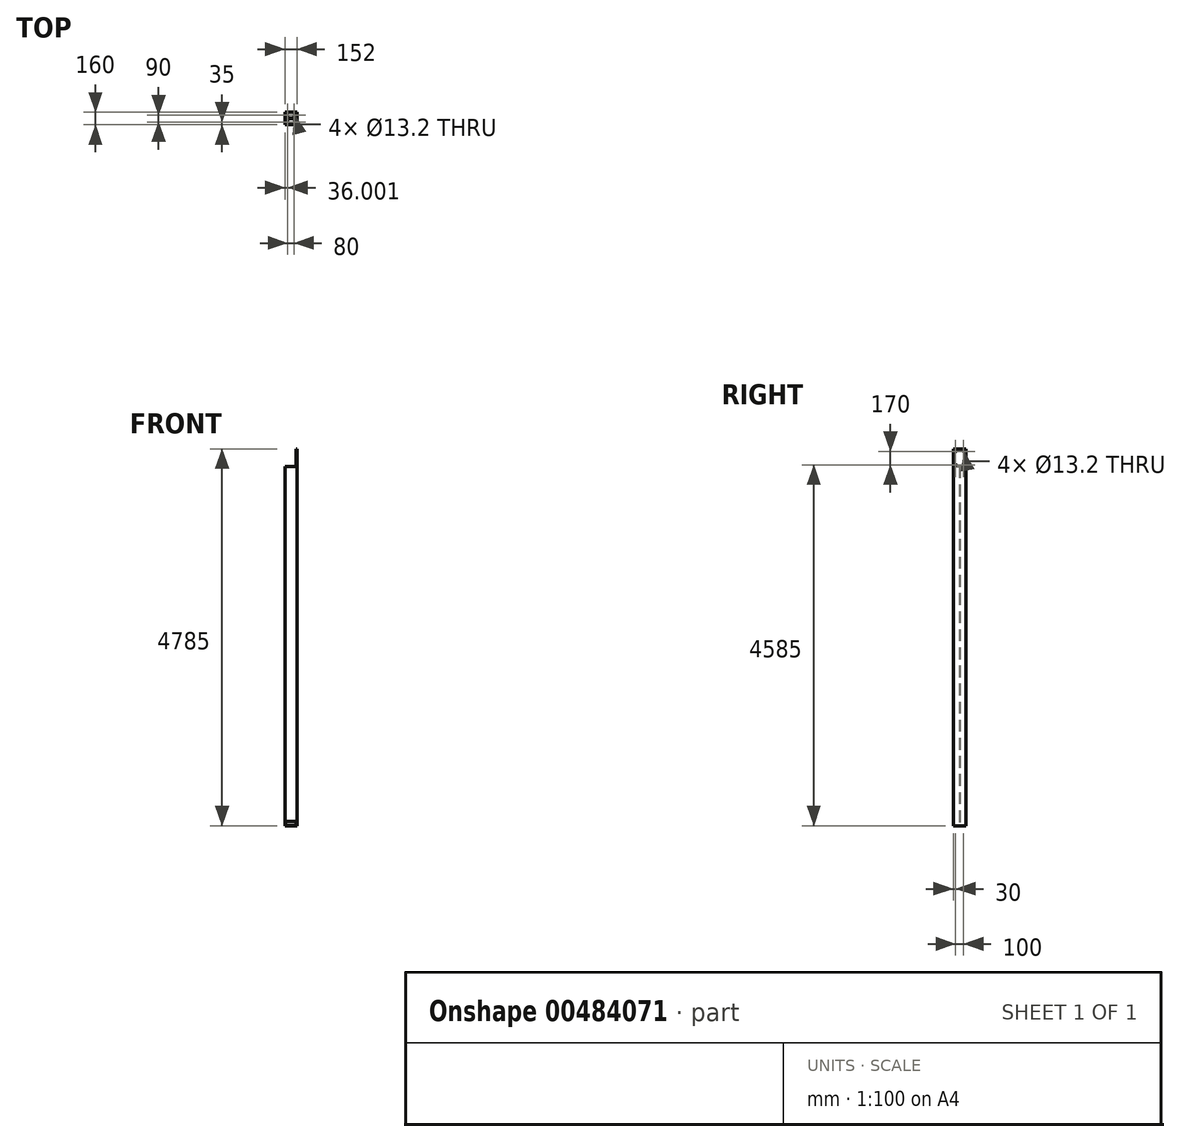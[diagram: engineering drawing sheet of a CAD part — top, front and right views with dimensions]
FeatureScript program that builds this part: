
annotation { "Feature Type Name" : "Feature", "Feature Type Description" : "" }
export const myFeature = defineFeature(function(context is Context, id is Id, definition is map)
    precondition{}
    {
        {
            var Q0;
            Q0=qCreatedBy(makeId("Top.planeOp"),FACE);
            var sketch = newSketch(context, id + "F0", { "sketchPlane" : qUnion([Q0])});
            skLineSegment(sketch, "E0", {"start": v(-170.58, -77) * mm, "end": v(-170.58, 83) * mm});
            skLineSegment(sketch, "E1", {"start": v(-170.58, 83) * mm, "end": v(-161.58, 83) * mm});
            skLineSegment(sketch, "E2", {"start": v(-161.58, 83) * mm, "end": v(-161.58, 6) * mm});
            skLineSegment(sketch, "E3", {"start": v(-161.58, 6) * mm, "end": v(-27.58, 6) * mm});
            skLineSegment(sketch, "E4", {"start": v(-27.58, 6) * mm, "end": v(-27.58, 83) * mm});
            skLineSegment(sketch, "E5", {"start": v(-27.58, 83) * mm, "end": v(-18.58, 83) * mm});
            skLineSegment(sketch, "E6", {"start": v(-18.58, 83) * mm, "end": v(-18.58, -77) * mm});
            skLineSegment(sketch, "E7", {"start": v(-18.58, -77) * mm, "end": v(-27.58, -77) * mm});
            skLineSegment(sketch, "E8", {"start": v(-27.58, -77) * mm, "end": v(-27.58, 0) * mm});
            skLineSegment(sketch, "E9", {"start": v(-27.58, 0) * mm, "end": v(-161.58, 0) * mm});
            skLineSegment(sketch, "E10", {"start": v(-161.58, 0) * mm, "end": v(-161.58, -77) * mm});
            skLineSegment(sketch, "E11", {"start": v(-161.58, -77) * mm, "end": v(-170.58, -77) * mm});
            skSolve(sketch);
        }
        {
            var Q0;
            Q0=qSketchRegion(id+"F0",true);
            extrude(context, id + "F1", {"entities" : qUnion([Q0]), "depth" : 4785 * mm, "offsetDistance" : 25 * mm});
        }
        {
            var Q0;
            Q0=makeQuery(id+"F1.opExtrude","SWEPT_FACE",FACE,{"disambiguationData":[OSD([sQuery(id+"F0.wireOp",EDGE,"E9")])]});
            var sketch = newSketch(context, id + "F2", { "sketchPlane" : qUnion([Q0])});
            skLineSegment(sketch, "E12.bottom", {"start": v(-161.58, 4785) * mm, "end": v(-27.58, 4785) * mm});
            skLineSegment(sketch, "E12.top", {"start": v(-161.58, 4565) * mm, "end": v(-27.58, 4565) * mm});
            skLineSegment(sketch, "E12.left", {"start": v(-161.58, 4785) * mm, "end": v(-161.58, 4565) * mm});
            skLineSegment(sketch, "E12.right", {"start": v(-27.58, 4785) * mm, "end": v(-27.58, 4565) * mm});
            skSolve(sketch);
        }
        {
            var Q0;
            Q0=qSketchRegion(id+"F2",true);
            extrude(context, id + "F3", {"entities" : qUnion([Q0]), "operationType" : NewBodyOperationType.REMOVE, "oppositeDirection" : true, "depth" : 100 * mm, "offsetDistance" : 25 * mm});
        }
        {
            var Q0;
            Q0=makeQuery(id+"F1.opExtrude","SWEPT_FACE",FACE,{"disambiguationData":[OSD([sQuery(id+"F0.wireOp",EDGE,"E0")])]});
            var sketch = newSketch(context, id + "F4", { "sketchPlane" : qUnion([Q0])});
            skLineSegment(sketch, "E13.bottom", {"start": v(-83, 4785) * mm, "end": v(77, 4785) * mm});
            skLineSegment(sketch, "E13.top", {"start": v(-83, 4565) * mm, "end": v(77, 4565) * mm});
            skLineSegment(sketch, "E13.left", {"start": v(-83, 4785) * mm, "end": v(-83, 4565) * mm});
            skLineSegment(sketch, "E13.right", {"start": v(77, 4785) * mm, "end": v(77, 4565) * mm});
            skSolve(sketch);
        }
        {
            var Q0;
            Q0=qSketchRegion(id+"F4",true);
            extrude(context, id + "F5", {"entities" : qUnion([Q0]), "operationType" : NewBodyOperationType.REMOVE, "oppositeDirection" : true, "depth" : 25 * mm, "offsetDistance" : 25 * mm});
        }
        {
            var Q0;
            Q0=makeQuery(id+"F1.opExtrude","SWEPT_FACE",FACE,{"disambiguationData":[OSD([sQuery(id+"F0.wireOp",EDGE,"E6")])]});
            var sketch = newSketch(context, id + "F6", { "sketchPlane" : qUnion([Q0])});
            skLineSegment(sketch, "E14", {"start": v(-77, 4785) * mm, "end": v(-47, 4785) * mm});
            skLineSegment(sketch, "E15", {"start": v(-47, 4785) * mm, "end": v(-47, 4755) * mm});
            skLineSegment(sketch, "E16", {"start": v(-47, 4755) * mm, "end": v(53, 4755) * mm});
            skLineSegment(sketch, "E17", {"start": v(53, 4755) * mm, "end": v(53, 4585) * mm});
            skLineSegment(sketch, "E18", {"start": v(53, 4585) * mm, "end": v(-47, 4585) * mm});
            skSolve(sketch);
        }
        {
            var Q0;
            Q0=sQuery(id+"F6.wireOp",VERTEX,"E16.start");
            var Q1;
            Q1=sQuery(id+"F6.wireOp",VERTEX,"E17.start");
            var Q2;
            Q2=sQuery(id+"F6.wireOp",VERTEX,"E18.end");
            var Q3;
            Q3=sQuery(id+"F6.wireOp",VERTEX,"E17.end");
            var Q4;
            Q4=makeQuery(id+"F1.opExtrude","SWEPT_BODY",BODY,{"disambiguationData":[OSD([sQuery(id+"F0.wireOp",EDGE,"E0"),sQuery(id+"F0.wireOp",EDGE,"E1"),sQuery(id+"F0.wireOp",EDGE,"E2"),sQuery(id+"F0.wireOp",EDGE,"E3"),sQuery(id+"F0.wireOp",EDGE,"E4"),sQuery(id+"F0.wireOp",EDGE,"E5"),sQuery(id+"F0.wireOp",EDGE,"E6"),sQuery(id+"F0.wireOp",EDGE,"E7"),sQuery(id+"F0.wireOp",EDGE,"E8"),sQuery(id+"F0.wireOp",EDGE,"E9"),sQuery(id+"F0.wireOp",EDGE,"E10"),sQuery(id+"F0.wireOp",EDGE,"E11")])]});
            hole(context, id + "F7", {"style" : HoleStyle.SIMPLE, "endStyle" : HoleEndStyle.THROUGH, "standardTappedOrClearance" : lookupTablePath({ "standard" : "ISO", "fit" : "Normal", "size" : "M12", "type" : "Clearance" }), "standardBlindInLast" : lookupTablePath({ "fit" : "Standard", "standard" : "ISO", "size" : "M12", "type" : "Clearance" }), "holeDiameter" : 13.2 * mm, "isTappedThrough" : true, "tappedDepth" : 12 * mm, "tapClearance" : 3, "locations" : qUnion([Q0, Q1, Q2, Q3]), "scope" : qUnion([Q4])});
        }
        {
            var Q0;
            Q0=makeQuery(id+"F1.opExtrude","SWEPT_FACE",FACE,{"disambiguationData":[OSD([sQuery(id+"F0.wireOp",EDGE,"E3")])]});
            var sketch = newSketch(context, id + "F8", { "sketchPlane" : qUnion([Q0])});
            skLineSegment(sketch, "E19.bottom", {"start": v(27.58, 0) * mm, "end": v(161.58, 0) * mm});
            skLineSegment(sketch, "E19.top", {"start": v(27.58, 5) * mm, "end": v(161.58, 5) * mm});
            skLineSegment(sketch, "E19.left", {"start": v(27.58, 0) * mm, "end": v(27.58, 5) * mm});
            skLineSegment(sketch, "E19.right", {"start": v(161.58, 0) * mm, "end": v(161.58, 5) * mm});
            skSolve(sketch);
        }
        {
            var Q0;
            Q0=qSketchRegion(id+"F8",true);
            extrude(context, id + "F9", {"entities" : qUnion([Q0]), "operationType" : NewBodyOperationType.ADD, "depth" : 77 * mm, "offsetDistance" : 25 * mm});
        }
        {
            var Q0;
            Q0=makeQuery(id+"F1.opExtrude","SWEPT_FACE",FACE,{"disambiguationData":[OSD([sQuery(id+"F0.wireOp",EDGE,"E9")])]});
            var sketch = newSketch(context, id + "F10", { "sketchPlane" : qUnion([Q0])});
            skLineSegment(sketch, "E20.bottom", {"start": v(-27.58, 0) * mm, "end": v(-161.58, 0) * mm});
            skLineSegment(sketch, "E20.top", {"start": v(-27.58, 5) * mm, "end": v(-161.58, 5) * mm});
            skLineSegment(sketch, "E20.left", {"start": v(-27.58, 0) * mm, "end": v(-27.58, 5) * mm});
            skLineSegment(sketch, "E20.right", {"start": v(-161.58, 0) * mm, "end": v(-161.58, 5) * mm});
            skSolve(sketch);
        }
        {
            var Q0;
            Q0=qSketchRegion(id+"F10",true);
            extrude(context, id + "F11", {"entities" : qUnion([Q0]), "operationType" : NewBodyOperationType.ADD, "depth" : 77 * mm, "offsetDistance" : 25 * mm});
        }
        {
            var Q0;
            Q0=makeQuery(id+"F11.boolean.opBoolean","MERGE",FACE,{"derivedFrom":[makeQuery(id+"F9.boolean.opBoolean","MERGE",FACE,{"derivedFrom":[makeQuery(id+"F1.opExtrude","CAP_FACE",FACE,{"disambiguationData":[OSD([sQuery(id+"F0.wireOp",EDGE,"E0"),sQuery(id+"F0.wireOp",EDGE,"E1"),sQuery(id+"F0.wireOp",EDGE,"E2"),sQuery(id+"F0.wireOp",EDGE,"E3"),sQuery(id+"F0.wireOp",EDGE,"E4"),sQuery(id+"F0.wireOp",EDGE,"E5"),sQuery(id+"F0.wireOp",EDGE,"E6"),sQuery(id+"F0.wireOp",EDGE,"E7"),sQuery(id+"F0.wireOp",EDGE,"E8"),sQuery(id+"F0.wireOp",EDGE,"E9"),sQuery(id+"F0.wireOp",EDGE,"E10"),sQuery(id+"F0.wireOp",EDGE,"E11")])],"isStart":true}),makeQuery(id+"F9.opExtrude","SWEPT_FACE",FACE,{"disambiguationData":[OSD([sQuery(id+"F8.wireOp",EDGE,"E19.bottom")])]})]}),makeQuery(id+"F11.opExtrude","SWEPT_FACE",FACE,{"disambiguationData":[OSD([sQuery(id+"F10.wireOp",EDGE,"E20.bottom")])]})]});
            var sketch = newSketch(context, id + "F12", { "sketchPlane" : qUnion([Q0])});
            skLineSegment(sketch, "E21", {"start": v(-94.58, -83) * mm, "end": v(-94.58, -48) * mm});
            skLineSegment(sketch, "E22", {"start": v(-94.58, -48) * mm, "end": v(-54.58, -48) * mm});
            skLineSegment(sketch, "E23", {"start": v(-94.58, -48) * mm, "end": v(-134.58, -48) * mm});
            skLineSegment(sketch, "E24", {"start": v(-94.58, 77) * mm, "end": v(-94.58, 42) * mm});
            skLineSegment(sketch, "E25", {"start": v(-94.58, 42) * mm, "end": v(-54.58, 42) * mm});
            skLineSegment(sketch, "E26", {"start": v(-94.58, 42) * mm, "end": v(-134.58, 42) * mm});
            skSolve(sketch);
        }
        {
            var Q0;
            Q0=sQuery(id+"F12.wireOp",VERTEX,"E22.end");
            var Q1;
            Q1=sQuery(id+"F12.wireOp",VERTEX,"E25.end");
            var Q2;
            Q2=sQuery(id+"F12.wireOp",VERTEX,"E26.end");
            var Q3;
            Q3=sQuery(id+"F12.wireOp",VERTEX,"E23.end");
            var Q4;
            Q4=makeQuery(id+"F1.opExtrude","SWEPT_BODY",BODY,{"disambiguationData":[OSD([sQuery(id+"F0.wireOp",EDGE,"E0"),sQuery(id+"F0.wireOp",EDGE,"E1"),sQuery(id+"F0.wireOp",EDGE,"E2"),sQuery(id+"F0.wireOp",EDGE,"E3"),sQuery(id+"F0.wireOp",EDGE,"E4"),sQuery(id+"F0.wireOp",EDGE,"E5"),sQuery(id+"F0.wireOp",EDGE,"E6"),sQuery(id+"F0.wireOp",EDGE,"E7"),sQuery(id+"F0.wireOp",EDGE,"E8"),sQuery(id+"F0.wireOp",EDGE,"E9"),sQuery(id+"F0.wireOp",EDGE,"E10"),sQuery(id+"F0.wireOp",EDGE,"E11")])]});
            hole(context, id + "F13", {"style" : HoleStyle.SIMPLE, "endStyle" : HoleEndStyle.THROUGH, "standardTappedOrClearance" : lookupTablePath({ "standard" : "ISO", "fit" : "Normal", "size" : "M12", "type" : "Clearance" }), "standardBlindInLast" : lookupTablePath({ "fit" : "Standard", "standard" : "ISO", "size" : "M12", "type" : "Clearance" }), "holeDiameter" : 13.2 * mm, "isTappedThrough" : true, "tappedDepth" : 12 * mm, "tapClearance" : 3, "locations" : qUnion([Q0, Q1, Q2, Q3]), "scope" : qUnion([Q4])});
        }
        {
            var Q0;
            Q0=makeQuery(id+"F11.boolean.opBoolean","MERGE",FACE,{"derivedFrom":[makeQuery(id+"F1.opExtrude","SWEPT_FACE",FACE,{"disambiguationData":[OSD([sQuery(id+"F0.wireOp",EDGE,"E7")])]}),makeQuery(id+"F1.opExtrude","SWEPT_FACE",FACE,{"disambiguationData":[OSD([sQuery(id+"F0.wireOp",EDGE,"E11")])]}),makeQuery(id+"F11.opExtrude","CAP_FACE",FACE,{"disambiguationData":[OSD([sQuery(id+"F10.wireOp",EDGE,"E20.bottom"),sQuery(id+"F10.wireOp",EDGE,"E20.top"),sQuery(id+"F10.wireOp",EDGE,"E20.left"),sQuery(id+"F10.wireOp",EDGE,"E20.right")])],"isStart":false})]});
            var sketch = newSketch(context, id + "F14", { "sketchPlane" : qUnion([Q0])});
            skLineSegment(sketch, "E27.bottom", {"start": v(-161.58, 4565) * mm, "end": v(-27.58, 4565) * mm});
            skLineSegment(sketch, "E27.top", {"start": v(-161.58, 55) * mm, "end": v(-27.58, 55) * mm});
            skLineSegment(sketch, "E27.left", {"start": v(-161.58, 4565) * mm, "end": v(-161.58, 55) * mm});
            skLineSegment(sketch, "E27.right", {"start": v(-27.58, 4565) * mm, "end": v(-27.58, 55) * mm});
            skSolve(sketch);
        }
        {
            var Q0;
            Q0=qSketchRegion(id+"F14",true);
            extrude(context, id + "F15", {"entities" : qUnion([Q0]), "operationType" : NewBodyOperationType.ADD, "depth" : -5 * mm, "offsetDistance" : 25 * mm});
        }
    });
